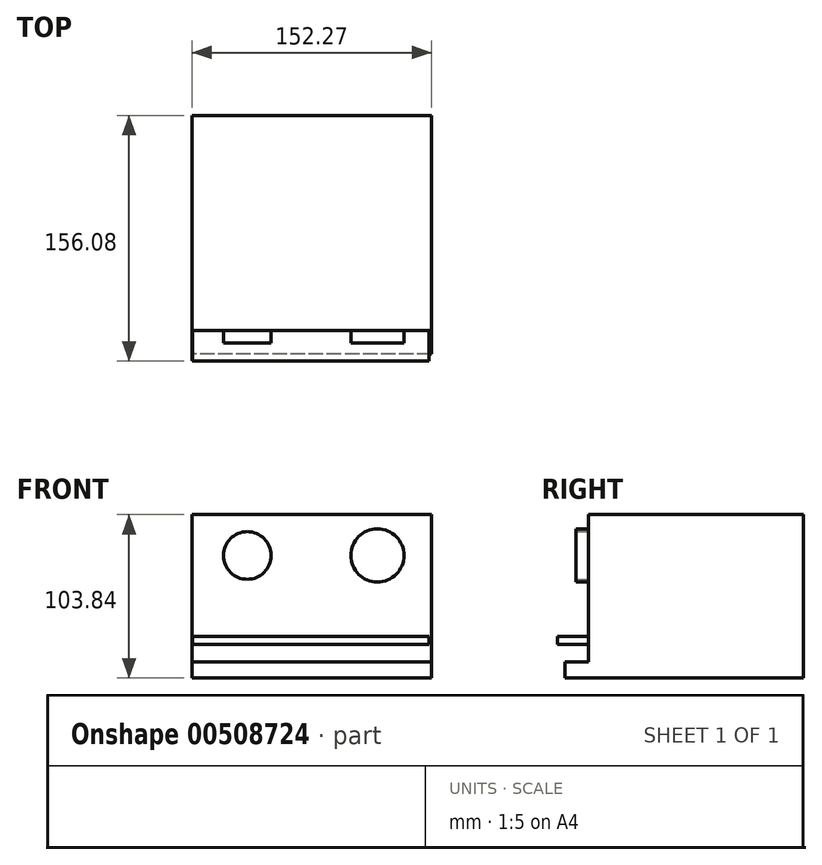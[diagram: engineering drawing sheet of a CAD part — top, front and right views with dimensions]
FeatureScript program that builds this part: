
annotation { "Feature Type Name" : "Feature", "Feature Type Description" : "" }
export const myFeature = defineFeature(function(context is Context, id is Id, definition is map)
    precondition{}
    {
        {
            var Q0;
            Q0=qCreatedBy(makeId("Top.planeOp"),FACE);
            var sketch = newSketch(context, id + "F0", { "sketchPlane" : qUnion([Q0])});
            skLineSegment(sketch, "E0.bottom", {"start": v(75.93, 75.3) * mm, "end": v(-76.34, 75.3) * mm});
            skLineSegment(sketch, "E0.top", {"start": v(75.93, -76.14) * mm, "end": v(-76.34, -76.14) * mm});
            skLineSegment(sketch, "E0.left", {"start": v(75.93, 75.3) * mm, "end": v(75.93, -76.14) * mm});
            skLineSegment(sketch, "E0.right", {"start": v(-76.34, 75.3) * mm, "end": v(-76.34, -76.14) * mm});
            skSolve(sketch);
        }
        {
            var Q0;
            Q0 = qSketchRegion(id + "F0", true);
            extrude(context, id + "F1", {"entities" : qUnion([Q0]), "oppositeDirection" : true, "depth" : 10.16 * mm});
        }
        {
            var Q0;
            Q0=makeQuery(id+"F1.opExtrude","CAP_FACE",FACE,{"disambiguationData":[OSD([sQuery(id+"F0.wireOp",EDGE,"E0.bottom"),sQuery(id+"F0.wireOp",EDGE,"E0.top"),sQuery(id+"F0.wireOp",EDGE,"E0.left"),sQuery(id+"F0.wireOp",EDGE,"E0.right")])],"isStart":true});
            var sketch = newSketch(context, id + "F2", { "sketchPlane" : qUnion([Q0])});
            skLineSegment(sketch, "E1.bottom", {"start": v(75.93, 75.3) * mm, "end": v(-76.34, 75.3) * mm});
            skLineSegment(sketch, "E1.top", {"start": v(75.93, -61.22) * mm, "end": v(-76.34, -61.22) * mm});
            skLineSegment(sketch, "E1.left", {"start": v(75.93, 75.3) * mm, "end": v(75.93, -61.22) * mm});
            skLineSegment(sketch, "E1.right", {"start": v(-76.34, 75.3) * mm, "end": v(-76.34, -61.22) * mm});
            skSolve(sketch);
        }
        {
            var Q0;
            Q0 = qSketchRegion(id + "F2", true);
            extrude(context, id + "F3", {"entities" : qUnion([Q0]), "operationType" : NewBodyOperationType.ADD, "depth" : 93.68 * mm});
        }
        {
            var Q0;
            Q0=makeQuery(id+"F3.opExtrude","SWEPT_FACE",FACE,{"disambiguationData":[OSD([sQuery(id+"F2.wireOp",EDGE,"E1.top")])]});
            var sketch = newSketch(context, id + "F4", { "sketchPlane" : qUnion([Q0])});
            skCircle(sketch, "E2", {"center": v(-41.2, 67.73) * mm, "radius": 15.12 * mm});
            skCircle(sketch, "E3", {"center": v(41.4, 67.73) * mm, "radius": 16.9 * mm});
            skSolve(sketch);
        }
        {
            var Q0;
            Q0 = qSketchRegion(id + "F4", true);
            extrude(context, id + "F5", {"entities" : qUnion([Q0]), "operationType" : NewBodyOperationType.ADD, "depth" : 7.96 * mm});
        }
        {
            var Q0;
            Q0=makeQuery(id+"F3.opExtrude","SWEPT_FACE",FACE,{"disambiguationData":[OSD([sQuery(id+"F2.wireOp",EDGE,"E1.top")])]});
            var sketch = newSketch(context, id + "F6", { "sketchPlane" : qUnion([Q0])});
            skSolve(sketch);
        }
        {
            var Q0;
            {var subQ0=sQuery(id+"F2.wireOp",EDGE,"E1.top");Q0=makeQuery(id+"F6.imprint","IMPRINT",FACE,{"disambiguationData":[TD([[makeQuery(id+"F6.imprint","IMPRINT",EDGE,{"derivedFrom":makeQuery(id+"F3.opExtrude","CAP_EDGE",EDGE,{"disambiguationData":[OSD([subQ0])],"isStart":false})}),1.0]])]});}
            var sketch = newSketch(context, id + "F7", { "sketchPlane" : qUnion([Q0])});
            skLineSegment(sketch, "E4.bottom", {"start": v(-76.32, 11.29) * mm, "end": v(74.19, 11.29) * mm});
            skLineSegment(sketch, "E4.top", {"start": v(-76.32, 11.16) * mm, "end": v(74.19, 11.16) * mm});
            skLineSegment(sketch, "E4.left", {"start": v(-76.32, 11.29) * mm, "end": v(-76.32, 11.16) * mm});
            skLineSegment(sketch, "E4.right", {"start": v(74.19, 11.29) * mm, "end": v(74.19, 11.16) * mm});
            skSolve(sketch);
        }
        {
            var Q0;
            Q0 = qSketchRegion(id + "F7", true);
            extrude(context, id + "F8", {"entities" : qUnion([Q0]), "operationType" : NewBodyOperationType.ADD, "depth" : 19.22 * mm});
        }
        {
            var Q0;
            {var subQ0=sQuery(id+"F2.wireOp",EDGE,"E1.top");Q0=makeQuery(id+"F6.imprint","IMPRINT",FACE,{"disambiguationData":[TD([[makeQuery(id+"F6.imprint","IMPRINT",EDGE,{"derivedFrom":makeQuery(id+"F3.opExtrude","CAP_EDGE",EDGE,{"disambiguationData":[OSD([subQ0])],"isStart":false})}),1.0]])]});}
            var sketch = newSketch(context, id + "F9", { "sketchPlane" : qUnion([Q0])});
            skLineSegment(sketch, "E5.bottom", {"start": v(-76.02, 16.36) * mm, "end": v(74.13, 16.36) * mm});
            skLineSegment(sketch, "E5.top", {"start": v(-76.02, 11.14) * mm, "end": v(74.13, 11.14) * mm});
            skLineSegment(sketch, "E5.left", {"start": v(-76.02, 16.36) * mm, "end": v(-76.02, 11.14) * mm});
            skLineSegment(sketch, "E5.right", {"start": v(74.13, 16.36) * mm, "end": v(74.13, 11.14) * mm});
            skSolve(sketch);
        }
        {
            var Q0;
            Q0 = qSketchRegion(id + "F9", true);
            extrude(context, id + "F10", {"entities" : qUnion([Q0]), "operationType" : NewBodyOperationType.ADD, "depth" : 19.55 * mm});
        }
    });
